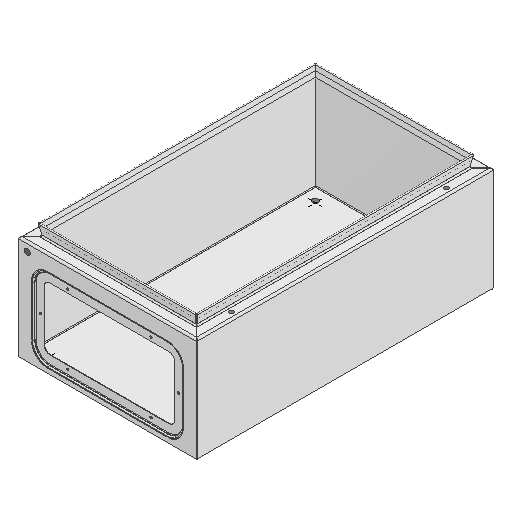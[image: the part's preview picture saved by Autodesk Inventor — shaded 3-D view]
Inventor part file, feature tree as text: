
AUTODESK INVENTOR PART (.ipt)
format: ipt  version: 2024.3 (Build 283343000, 343)  size: 579,072 bytes
history: native  units: in
note: dims shown in document units (in); Inventor stores cm internally (conversion verified against a paired STEP export)
features: sketch x1, imported_body x1
ambient origin geometry x8: Origin, YZ Plane, XZ Plane, XY Plane, X Axis, Y Axis, Z Axis, Center Point
bodies: Solid1 (feature_tree)
feature tree (2):
  sketch  "Sketch1"
  imported_body  "Base1"
